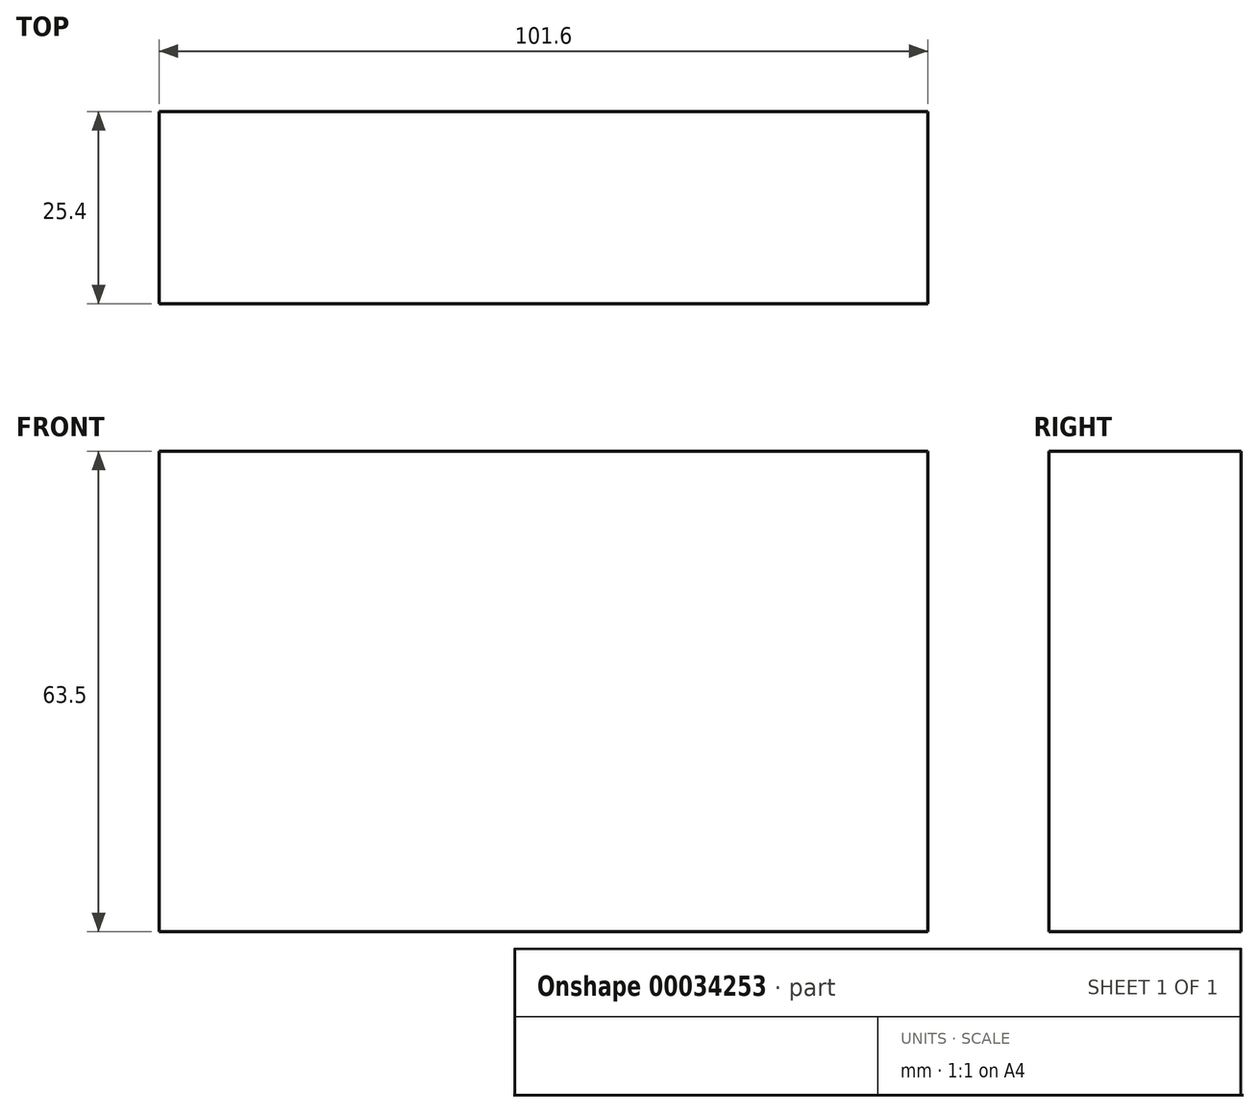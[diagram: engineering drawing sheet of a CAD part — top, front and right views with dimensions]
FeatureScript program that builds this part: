
annotation { "Feature Type Name" : "Feature", "Feature Type Description" : "" }
export const myFeature = defineFeature(function(context is Context, id is Id, definition is map)
    precondition{}
    {
        {
            var Q0;
            Q0=qCreatedBy(makeId("Front.planeOp"),FACE);
            var sketch = newSketch(context, id + "F0", { "sketchPlane" : qUnion([Q0])});
            skLineSegment(sketch, "E0.bottom", {"start": v(0, 0) * mm, "end": v(101.6, 0) * mm});
            skLineSegment(sketch, "E0.top", {"start": v(0, 63.5) * mm, "end": v(101.6, 63.5) * mm});
            skLineSegment(sketch, "E0.left", {"start": v(0, 0) * mm, "end": v(0, 63.5) * mm});
            skLineSegment(sketch, "E0.right", {"start": v(101.6, 0) * mm, "end": v(101.6, 63.5) * mm});
            skSolve(sketch);
        }
        {
            var Q0;
            Q0 = qSketchRegion(id + "F0", true);
            extrude(context, id + "F1", {"entities" : qUnion([Q0]), "depth" : 25.4 * mm});
        }
    });
